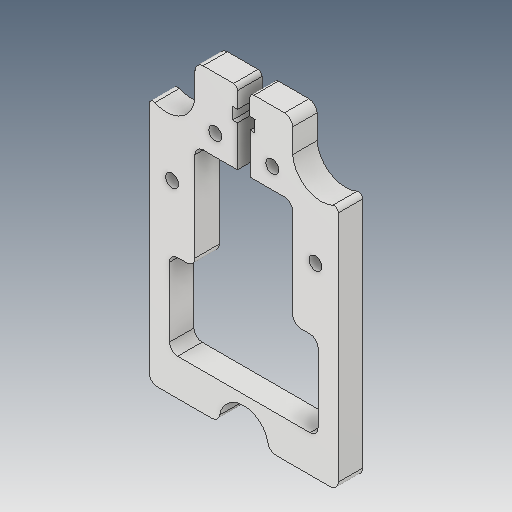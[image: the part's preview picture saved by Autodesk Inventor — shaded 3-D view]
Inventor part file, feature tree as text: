
AUTODESK INVENTOR PART (.ipt)
format: ipt  version: 2017 (Build 210142000, 142)  size: 192,512 bytes
history: native  units: in
note: dims shown in document units (in); Inventor stores cm internally (conversion verified against a paired STEP export)
features: extrude x2, sketch x2, fillet x1
ambient origin geometry x8: Origin, YZ Plane, XZ Plane, XY Plane, X Axis, Y Axis, Z Axis, Center Point
bodies: Solid1 (feature_tree)
feature tree (5):
  extrude  "Extrusion1"  Depth=0.0787in
  extrude  "Extrusion2"  Depth=0.0787in
  fillet  "Fillet1"  Radius=0.2362in
  sketch  "Sketch1"  dims[d0=1.2205in d1=0.2756in d2=0.2756in d6=0.0787in]
  sketch  "Sketch2"  dims[d8=1.1811in d13=0.0787in d14=0.2362in d15=0.0in d16=0.1575in d17=0.2362in d18=0.0in d19=0.0787in]
